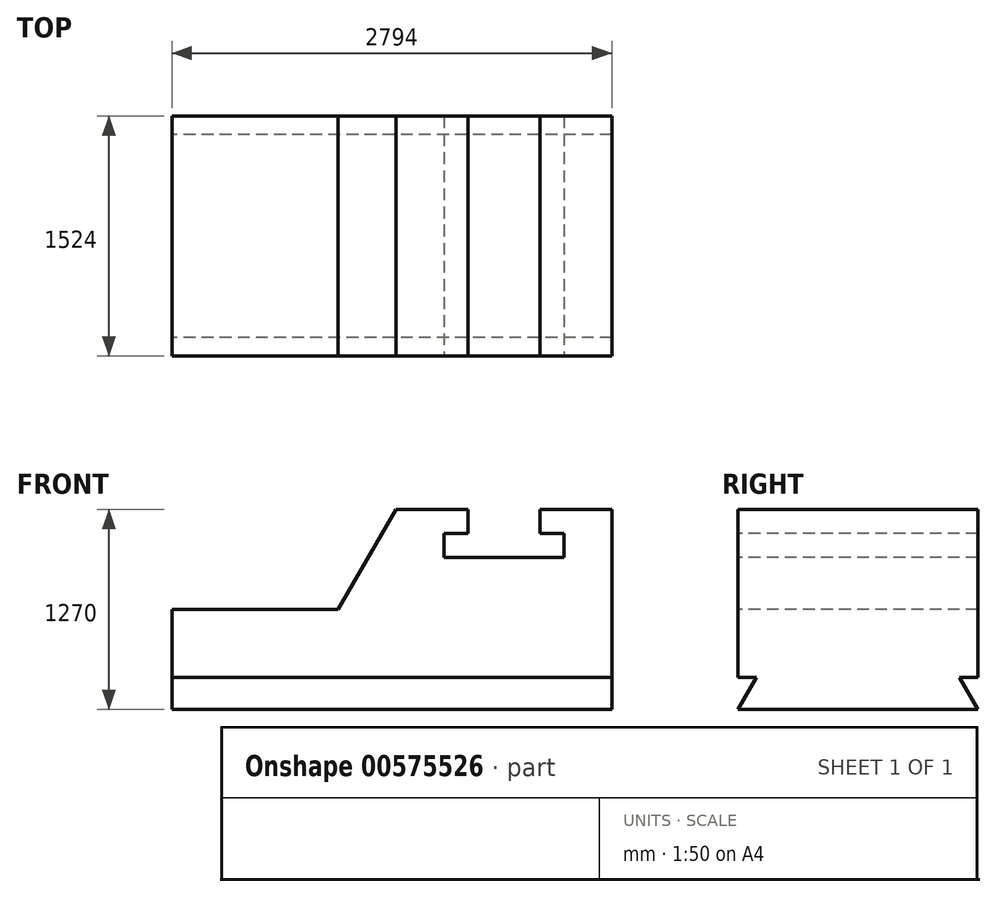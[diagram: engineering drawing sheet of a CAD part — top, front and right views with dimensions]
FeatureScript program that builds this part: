
annotation { "Feature Type Name" : "Feature", "Feature Type Description" : "" }
export const myFeature = defineFeature(function(context is Context, id is Id, definition is map)
    precondition{}
    {
        {
            var Q0;
            Q0=qCreatedBy(makeId("Front.planeOp"),FACE);
            var sketch = newSketch(context, id + "F0", { "sketchPlane" : qUnion([Q0])});
            skLineSegment(sketch, "E0.bottom", {"start": v(0, 0) * mm, "end": v(2794, 0) * mm});
            skLineSegment(sketch, "E0.top", {"start": v(0, 1270) * mm, "end": v(2794, 1270) * mm});
            skLineSegment(sketch, "E0.left", {"start": v(0, 0) * mm, "end": v(0, 1270) * mm});
            skLineSegment(sketch, "E0.right", {"start": v(2794, 0) * mm, "end": v(2794, 1270) * mm});
            skSolve(sketch);
        }
        {
            var Q0;
            Q0=makeQuery(id+"F0.imprint","IMPRINT",FACE,{"disambiguationData":[TD([[makeQuery(id+"F0.imprint","IMPRINT",EDGE,{"derivedFrom":sQuery(id+"F0.wireOp",EDGE,"E0.bottom")}),1.0]])]});
            extrude(context, id + "F1", {"entities" : qUnion([Q0]), "depth" : 1524 * mm, "offsetDistance" : 25.4 * mm});
        }
        {
            var Q0;
            Q0=makeQuery(id+"F1.opExtrude","CAP_FACE",FACE,{"disambiguationData":[OSD([sQuery(id+"F0.wireOp",EDGE,"E0.bottom"),sQuery(id+"F0.wireOp",EDGE,"E0.top"),sQuery(id+"F0.wireOp",EDGE,"E0.left"),sQuery(id+"F0.wireOp",EDGE,"E0.right")])],"isStart":false});
            var sketch = newSketch(context, id + "F2", { "sketchPlane" : qUnion([Q0])});
            skLineSegment(sketch, "E1.bottom", {"start": v(1727.2, 1117.6) * mm, "end": v(2489.2, 1117.6) * mm});
            skLineSegment(sketch, "E1.top", {"start": v(1727.2, 965.2) * mm, "end": v(2489.2, 965.2) * mm});
            skLineSegment(sketch, "E1.left", {"start": v(1727.2, 1117.6) * mm, "end": v(1727.2, 965.2) * mm});
            skLineSegment(sketch, "E1.right", {"start": v(2489.2, 1117.6) * mm, "end": v(2489.2, 965.2) * mm});
            skSolve(sketch);
        }
        {
            var Q0;
            Q0=makeQuery(id+"F2.imprint","IMPRINT",FACE,{"disambiguationData":[TD([[makeQuery(id+"F2.imprint","IMPRINT",EDGE,{"derivedFrom":sQuery(id+"F2.wireOp",EDGE,"E1.bottom")}),-1.0]])]});
            extrude(context, id + "F3", {"entities" : qUnion([Q0]), "operationType" : NewBodyOperationType.REMOVE, "endBound" : BoundingType.THROUGH_ALL, "oppositeDirection" : true, "depth" : 25.4 * mm, "offsetDistance" : 25.4 * mm});
        }
        {
            var Q0;
            Q0=makeQuery(id+"F1.opExtrude","CAP_FACE",FACE,{"disambiguationData":[OSD([sQuery(id+"F0.wireOp",EDGE,"E0.bottom"),sQuery(id+"F0.wireOp",EDGE,"E0.top"),sQuery(id+"F0.wireOp",EDGE,"E0.left"),sQuery(id+"F0.wireOp",EDGE,"E0.right")])],"isStart":false});
            var sketch = newSketch(context, id + "F4", { "sketchPlane" : qUnion([Q0])});
            skLineSegment(sketch, "E2.bottom", {"start": v(1879.6, 1509.94) * mm, "end": v(2336.8, 1509.94) * mm});
            skLineSegment(sketch, "E2.top", {"start": v(1879.6, 1067.46) * mm, "end": v(2336.8, 1067.46) * mm});
            skLineSegment(sketch, "E2.left", {"start": v(1879.6, 1509.94) * mm, "end": v(1879.6, 1067.46) * mm});
            skLineSegment(sketch, "E2.right", {"start": v(2336.8, 1509.94) * mm, "end": v(2336.8, 1067.46) * mm});
            skSolve(sketch);
        }
        {
            var Q0;
            {var subQ0=sQuery(id+"F4.wireOp",EDGE,"E2.left");var subQ1=makeQuery(id+"F1.opExtrude","CAP_EDGE",EDGE,{"disambiguationData":[OSD([sQuery(id+"F0.wireOp",EDGE,"E0.top")])],"isStart":false});var subQ2=makeQuery(id+"F4.imprint","INTERSECT",VERTEX,{"derivedFrom":[subQ1,subQ0]});Q0=makeQuery(id+"F4.imprint","IMPRINT",FACE,{"disambiguationData":[TD([[makeQuery(id+"F4.imprint","IMPRINT",EDGE,{"disambiguationData":[TD([[subQ2,-1.0]])],"derivedFrom":subQ0}),1.0]])]});}
            extrude(context, id + "F5", {"entities" : qUnion([Q0]), "operationType" : NewBodyOperationType.REMOVE, "endBound" : BoundingType.THROUGH_ALL, "oppositeDirection" : true, "depth" : 25.4 * mm, "offsetDistance" : 25.4 * mm});
        }
        {
            var Q0;
            Q0=makeQuery(id+"F1.opExtrude","CAP_FACE",FACE,{"disambiguationData":[OSD([sQuery(id+"F0.wireOp",EDGE,"E0.bottom"),sQuery(id+"F0.wireOp",EDGE,"E0.top"),sQuery(id+"F0.wireOp",EDGE,"E0.left"),sQuery(id+"F0.wireOp",EDGE,"E0.right")])],"isStart":false});
            var sketch = newSketch(context, id + "F6", { "sketchPlane" : qUnion([Q0])});
            skLineSegment(sketch, "E3", {"start": v(1879.6, 1270) * mm, "end": v(1422.4, 1270) * mm});
            skLineSegment(sketch, "E4", {"start": v(1422.4, 1270) * mm, "end": v(1055.78, 635) * mm});
            skLineSegment(sketch, "E5", {"start": v(0, 0) * mm, "end": v(0, 635) * mm});
            skLineSegment(sketch, "E6", {"start": v(0, 635) * mm, "end": v(1055.78, 635) * mm});
            skSolve(sketch);
        }
        {
            var Q0;
            {var subQ0=sQuery(id+"F6.wireOp",EDGE,"E4");Q0=makeQuery(id+"F6.imprint","IMPRINT",FACE,{"disambiguationData":[TD([[makeQuery(id+"F6.imprint","IMPRINT",EDGE,{"derivedFrom":subQ0}),-1.0]])]});}
            extrude(context, id + "F7", {"entities" : qUnion([Q0]), "operationType" : NewBodyOperationType.REMOVE, "endBound" : BoundingType.THROUGH_ALL, "oppositeDirection" : true, "depth" : 25.4 * mm, "offsetDistance" : 25.4 * mm});
        }
        {
            var Q0;
            Q0=makeQuery(id+"F1.opExtrude","SWEPT_FACE",FACE,{"disambiguationData":[OSD([sQuery(id+"F0.wireOp",EDGE,"E0.left")])]});
            var sketch = newSketch(context, id + "F8", { "sketchPlane" : qUnion([Q0])});
            skLineSegment(sketch, "E7", {"start": v(1524, 0) * mm, "end": v(1406.68, 203.2) * mm});
            skLineSegment(sketch, "E8", {"start": v(1524, 0) * mm, "end": v(1524, 203.2) * mm});
            skLineSegment(sketch, "E9", {"start": v(1524, 203.2) * mm, "end": v(1406.68, 203.2) * mm});
            skSolve(sketch);
        }
        {
            var Q0;
            Q0=makeQuery(id+"F8.imprint","IMPRINT",FACE,{"disambiguationData":[TD([[makeQuery(id+"F8.imprint","IMPRINT",EDGE,{"derivedFrom":sQuery(id+"F8.wireOp",EDGE,"E7")}),-1.0]])]});
            extrude(context, id + "F9", {"entities" : qUnion([Q0]), "operationType" : NewBodyOperationType.REMOVE, "endBound" : BoundingType.THROUGH_ALL, "oppositeDirection" : true, "depth" : 25.4 * mm, "offsetDistance" : 25.4 * mm});
        }
        {
            var Q0;
            Q0=makeQuery(id+"F1.opExtrude","SWEPT_FACE",FACE,{"disambiguationData":[OSD([sQuery(id+"F0.wireOp",EDGE,"E0.left")])]});
            var sketch = newSketch(context, id + "F10", { "sketchPlane" : qUnion([Q0])});
            skLineSegment(sketch, "E10", {"start": v(0, 0) * mm, "end": v(117.32, 203.2) * mm});
            skLineSegment(sketch, "E11", {"start": v(0, 0) * mm, "end": v(0, 203.2) * mm});
            skLineSegment(sketch, "E12", {"start": v(0, 203.2) * mm, "end": v(117.32, 203.2) * mm});
            skSolve(sketch);
        }
        {
            var Q0;
            Q0=makeQuery(id+"F10.imprint","IMPRINT",FACE,{"disambiguationData":[TD([[makeQuery(id+"F10.imprint","IMPRINT",EDGE,{"derivedFrom":sQuery(id+"F10.wireOp",EDGE,"E10")}),1.0]])]});
            extrude(context, id + "F11", {"entities" : qUnion([Q0]), "operationType" : NewBodyOperationType.REMOVE, "endBound" : BoundingType.THROUGH_ALL, "oppositeDirection" : true, "depth" : 25.4 * mm, "offsetDistance" : 25.4 * mm});
        }
    });
